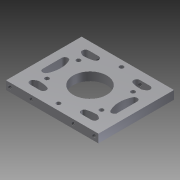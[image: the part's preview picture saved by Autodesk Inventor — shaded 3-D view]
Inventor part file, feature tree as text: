
AUTODESK INVENTOR PART (.ipt)
format: ipt  version: 2012 (Build 160160000, 160)  size: 306,688 bytes
history: native  units: in
note: dims shown in document units (in); Inventor stores cm internally (conversion verified against a paired STEP export)
features: thread x6, sketch x5, hole x4, extrude x3, fillet x2, plane x1, projected_geometry x1
ambient origin geometry x8: Origin, YZ Plane, XZ Plane, XY Plane, X Axis, Y Axis, Z Axis, Center Point
bodies: Solid1 (feature_tree)
feature tree (22):
  sketch  "Sketch1"  dims[d0=1.375in d1=2.75in]
  extrude  "Extrusion1"  Depth=2.75in
  hole  "Hole6"  [1 undecoded]
  plane  "Work Plane5"
  extrude  "Extrusion6"  Depth=0.25in TaperAngle=0.0deg
  fillet  "Fillet1"  Radius=1.875in
  sketch  "Sketch13"  dims[d4=1.0in d6=0.25in d7=0.0in d139=1.875in]
  sketch  "Sketch14"  dims[d140=2.3622in d142=360.0deg]
  hole  "Hole8"  [1 undecoded]
  thread  "Thread9"  [1 undecoded]
  thread  "Thread11"  [1 undecoded]
  hole  "Hole11"  [1 undecoded]
  hole  "Hole12"  [1 undecoded]
  thread  "Thread13"  [1 undecoded]
  thread  "Thread14"  [1 undecoded]
  thread  "Thread15"  [1 undecoded]
  thread  "Thread16"  [1 undecoded]
  extrude  "Extrusion8"  Depth=0.25in
  fillet  "Fillet5"  Radius=0.125in
  sketch  "Sketch12"  dims[d2=2.25in d3=1.125in]
  projected_geometry  "Projected Loop1"
  sketch  "Sketch16"  dims[d144=0.125in d145=0.75in d146=0.1875in d147=0.25in d148=0.5635in d149=1.0in d150=0.8108in d160=-0.125in d161=0.1875in d162=1.0in d168=0.25in d169=0.25in d170=0.25in d171=0.125in d173=0.125in d174=0.25in d175=0.25in d176=0.125in d177=0.25in d178=0.125in d179=0.1875in d180=1.0in d181=0.1875in d182=1.0in d183=0.1875in d184=1.0in d185=0.1875in d186=0.1875in d187=1.0in d188=1.0in d189=1.0in d190=0.0in d191=0.0625in d192=0.25in d193=0.25in d194=0.25in d195=0.25in d197=0.1875in d198=0.75in d199=0.125in d200=0.125in d201=0.125in d202=0.125in d203=0.125in d204=0.125in d205=0.125in d206=0.125in d211=0.125in d212=0.125in d213=0.125in d214=0.125in d215=0.106in d216=0.75in d217=0.375in d218=0.25in d219=0.5635in d220=1.0in d221=0.8108in d240=1.0in d241=0.0in d244=1.0in d245=0.0in d251=0.7504in d252=0.75in d253=0.106in d254=0.75in d255=0.375in d256=0.25in d257=0.5635in d258=0.3in d259=0.8108in d260=0.75in d261=0.75in d262=0.106in d263=0.75in d264=0.375in d265=0.25in d266=0.5635in d267=0.3in d268=0.8108in d269=1.0in d270=0.0in d271=1.0in d272=0.0in d273=1.0in d274=0.0in d275=1.0in d276=0.0in d277=90.0deg d278=45.0deg d289=0.25in d290=0.25in d291=1.0in d292=0.0in d293=0.0938in d294=0.25in d295=0.125in d296=0.25in d297=0.125in d45=1.0in d46=1.0in d132=1.0in d133=1.0in]
note: 10 required parameter values undecoded (feature->parameter linkage not recoverable at this tier; creation-order binding heuristic only, values carry confidence <= 0.55)
